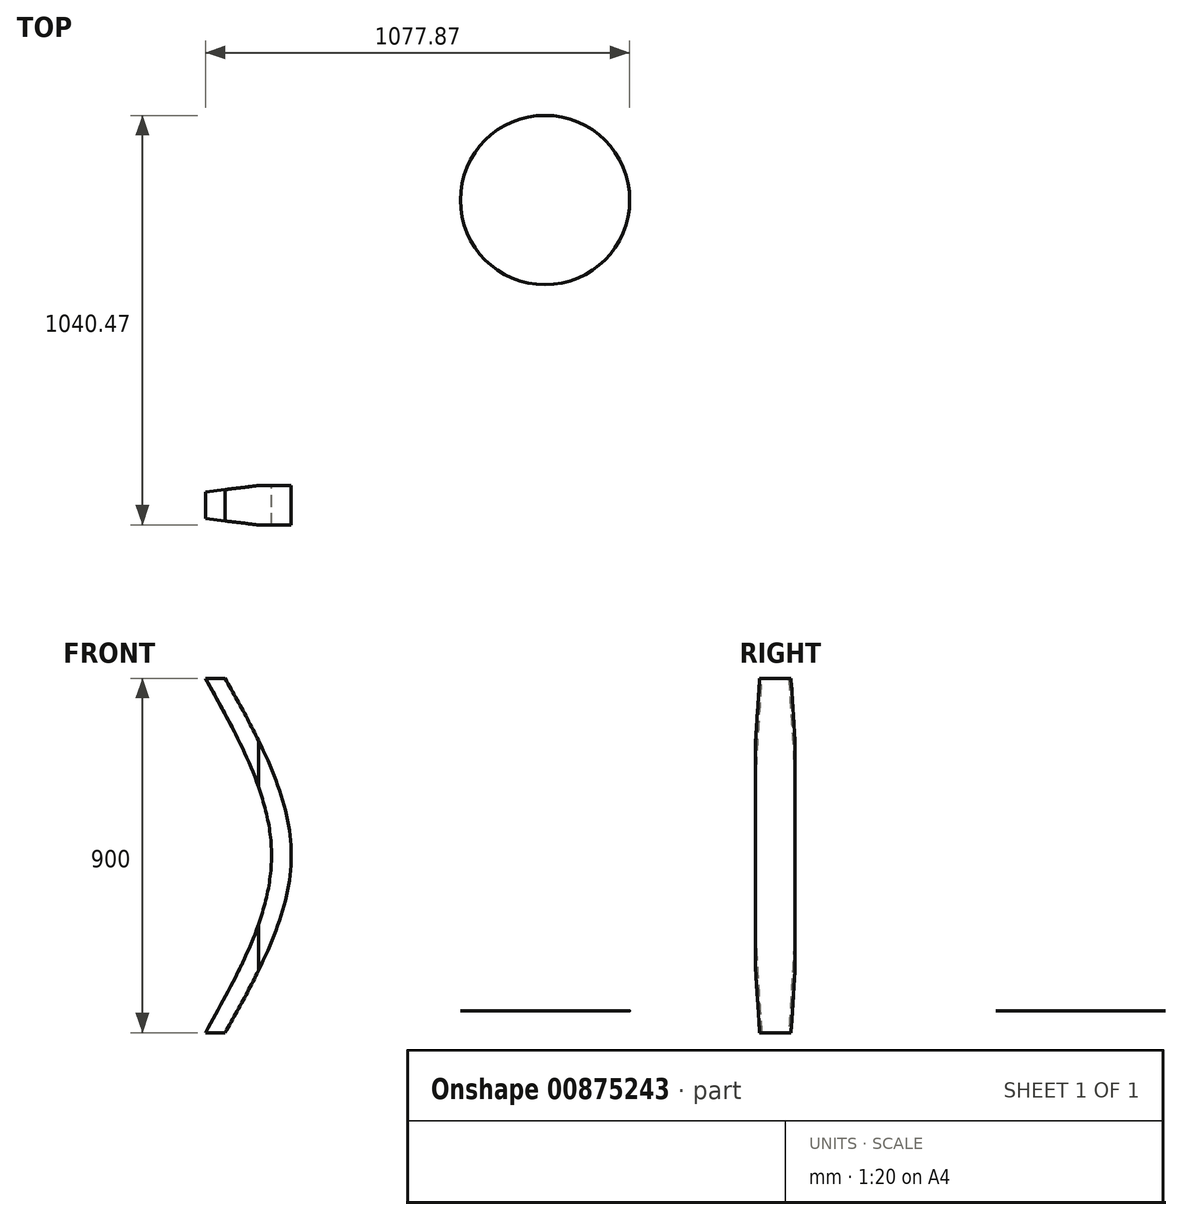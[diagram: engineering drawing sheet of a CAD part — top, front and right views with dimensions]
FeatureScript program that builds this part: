
annotation { "Feature Type Name" : "Feature", "Feature Type Description" : "" }
export const myFeature = defineFeature(function(context is Context, id is Id, definition is map)
    precondition{}
    {
        {
            var Q0;
            Q0=qCreatedBy(makeId("Right.planeOp"),FACE);
            var sketch = newSketch(context, id + "F0", { "sketchPlane" : qUnion([Q0])});
            skLineSegment(sketch, "E0.bottom", {"start": v(-21.22, 845.17) * mm, "end": v(78.78, 845.17) * mm});
            skLineSegment(sketch, "E0.top", {"start": v(-21.22, -54.83) * mm, "end": v(78.78, -54.83) * mm});
            skLineSegment(sketch, "E0.left", {"start": v(-21.22, 845.17) * mm, "end": v(-21.22, -54.83) * mm});
            skLineSegment(sketch, "E0.right", {"start": v(78.78, 845.17) * mm, "end": v(78.78, -54.83) * mm});
            skSolve(sketch);
        }
        {
            var Q0;
            Q0 = qSketchRegion(id + "F0", true);
            extrude(context, id + "F1", {"entities" : qUnion([Q0]), "depth" : 187.9 * mm, "offsetDistance" : 25 * mm});
        }
        {
            var Q0;
            Q0=makeQuery(id+"F1.opExtrude","CAP_FACE",FACE,{"disambiguationData":[OSD([sQuery(id+"F0.wireOp",EDGE,"E0.bottom"),sQuery(id+"F0.wireOp",EDGE,"E0.top"),sQuery(id+"F0.wireOp",EDGE,"E0.left"),sQuery(id+"F0.wireOp",EDGE,"E0.right")])],"isStart":true});
            extrude(context, id + "F2", {"entities" : qUnion([Q0]), "operationType" : NewBodyOperationType.ADD, "depth" : 30 * mm, "offsetDistance" : 25 * mm});
        }
        {
            var Q0;
            Q0=makeQuery(id+"F1.opExtrude","SWEPT_FACE",FACE,{"disambiguationData":[OSD([sQuery(id+"F0.wireOp",EDGE,"E0.right")])]});
            var sketch = newSketch(context, id + "F3", { "sketchPlane" : qUnion([Q0])});
            skLineSegment(sketch, "E1", {"start": v(-187.9, 395.17) * mm, "end": v(0, 395.17) * mm});
            skLineSegment(sketch, "E2", {"start": v(-187.9, 845.17) * mm, "end": v(-20, 845.17) * mm});
            skLineSegment(sketch, "E3", {"start": v(-20, -54.83) * mm, "end": v(-187.9, -54.83) * mm});
            skLineSegment(sketch, "E4", {"start": v(-187.9, -54.83) * mm, "end": v(-187.9, 395.17) * mm});
            skLineSegment(sketch, "E5", {"start": v(-187.9, 845.17) * mm, "end": v(-187.9, 395.17) * mm});
            skLineSegment(sketch, "E6", {"start": v(0, -54.83) * mm, "end": v(-20, -54.83) * mm});
            skLineSegment(sketch, "E7", {"start": v(-187.9, 395.17) * mm, "end": v(-137.9, 395.17) * mm});
            skFitSpline(sketch, "E8", {"points": [v(-20, -54.83) * mm, v(-187.9, 395.17) * mm, v(-20, 845.17) * mm], "startDerivative": vector(-503.7, 900) * mm, "endDerivative": vector(503.7, 900) * mm});
            skLineSegment(sketch, "E9", {"start": v(-20, 845.17) * mm, "end": v(30, 845.17) * mm});
            skLineSegment(sketch, "E10", {"start": v(30, 845.17) * mm, "end": v(30, -54.83) * mm});
            skLineSegment(sketch, "E11", {"start": v(30, -54.83) * mm, "end": v(-20, -54.83) * mm});
            skFitSpline(sketch, "E12", {"points": [v(30, -54.83) * mm, v(-137.9, 395.17) * mm, v(30, 845.17) * mm], "startDerivative": vector(-503.7, 900) * mm, "endDerivative": vector(503.7, 900) * mm});
            skSolve(sketch);
        }
        {
            var Q0;
            {var subQ0=sQuery(id+"F3.wireOp",EDGE,"E2");Q0=makeQuery(id+"F3.imprint","IMPRINT",FACE,{"disambiguationData":[TD([[makeQuery(id+"F3.imprint","IMPRINT",EDGE,{"derivedFrom":subQ0}),-1.0]])]});}
            var Q1;
            {var subQ0=sQuery(id+"F3.wireOp",EDGE,"E3");Q1=makeQuery(id+"F3.imprint","IMPRINT",FACE,{"disambiguationData":[TD([[makeQuery(id+"F3.imprint","IMPRINT",EDGE,{"derivedFrom":subQ0}),1.0]])]});}
            var Q2;
            {var subQ0=sQuery(id+"F3.wireOp",EDGE,"E10");Q2=makeQuery(id+"F3.imprint","IMPRINT",FACE,{"disambiguationData":[TD([[makeQuery(id+"F3.imprint","IMPRINT",EDGE,{"derivedFrom":subQ0}),-1.0]])]});}
            extrude(context, id + "F4", {"entities" : qUnion([Q0, Q1, Q2]), "operationType" : NewBodyOperationType.REMOVE, "oppositeDirection" : true, "depth" : 600 * mm, "offsetDistance" : 25 * mm});
        }
        {
            var Q0;
            {var subQ0=sQuery(id+"F0.wireOp",EDGE,"E0.bottom");Q0=makeQuery(id+"F2.boolean.opBoolean","MERGE",FACE,{"derivedFrom":[makeQuery(id+"F1.opExtrude","SWEPT_FACE",FACE,{"disambiguationData":[OSD([subQ0])]}),makeQuery(id+"F2.opExtrude","SWEPT_FACE",FACE,{"disambiguationData":[OSD([subQ0])]})]});}
            var sketch = newSketch(context, id + "F5", { "sketchPlane" : qUnion([Q0])});
            skLineSegment(sketch, "E13", {"start": v(-30, 28.78) * mm, "end": v(-30, 62.53) * mm});
            skLineSegment(sketch, "E14", {"start": v(-30, 28.78) * mm, "end": v(-30, -4.98) * mm});
            skLineSegment(sketch, "E15", {"start": v(319.35, 247.93) * mm, "end": v(319.35, -262.5) * mm});
            skLineSegment(sketch, "E16", {"start": v(-30, -4.98) * mm, "end": v(-30, -262.5) * mm});
            skLineSegment(sketch, "E17", {"start": v(-30, -262.5) * mm, "end": v(319.35, -262.5) * mm});
            skLineSegment(sketch, "E18", {"start": v(319.35, 247.93) * mm, "end": v(-30, 247.93) * mm});
            skLineSegment(sketch, "E19", {"start": v(-30, 247.93) * mm, "end": v(-30, 62.53) * mm});
            skLineSegment(sketch, "E20", {"start": v(20, 28.78) * mm, "end": v(187.9, 28.78) * mm});
            skLineSegment(sketch, "E21", {"start": v(187.9, 28.78) * mm, "end": v(187.9, -31.22) * mm});
            skLineSegment(sketch, "E22", {"start": v(187.9, -31.22) * mm, "end": v(187.9, 88.78) * mm});
            skLineSegment(sketch, "E23", {"start": v(187.9, 88.78) * mm, "end": v(-30, 62.53) * mm});
            skLineSegment(sketch, "E24", {"start": v(-30, -4.98) * mm, "end": v(187.9, -31.22) * mm});
            skSolve(sketch);
        }
        {
            var Q0;
            {var subQ1=sQuery(id+"F0.wireOp",EDGE,"E0.right");var subQ2=sQuery(id+"F0.wireOp",EDGE,"E0.bottom");var subQ3=makeQuery(id+"F2.boolean.opBoolean","MERGE",EDGE,{"derivedFrom":[makeQuery(id+"F1.opExtrude","SWEPT_EDGE",EDGE,{"disambiguationData":[OSD([subQ2,subQ1])]}),makeQuery(id+"F2.opExtrude","SWEPT_EDGE",EDGE,{"disambiguationData":[OSD([subQ2,subQ1])]})]});Q0=makeQuery(id+"F5.imprint","IMPRINT",FACE,{"disambiguationData":[TD([[makeQuery(id+"F5.imprint","IMPRINT",EDGE,{"derivedFrom":subQ3}),1.0]])]});}
            var Q1;
            {var subQ1=sQuery(id+"F0.wireOp",EDGE,"E0.left");var subQ2=sQuery(id+"F0.wireOp",EDGE,"E0.bottom");var subQ3=makeQuery(id+"F2.boolean.opBoolean","MERGE",EDGE,{"derivedFrom":[makeQuery(id+"F1.opExtrude","SWEPT_EDGE",EDGE,{"disambiguationData":[OSD([subQ2,subQ1])]}),makeQuery(id+"F2.opExtrude","SWEPT_EDGE",EDGE,{"disambiguationData":[OSD([subQ2,subQ1])]})]});Q1=makeQuery(id+"F5.imprint","IMPRINT",FACE,{"disambiguationData":[TD([[makeQuery(id+"F5.imprint","IMPRINT",EDGE,{"derivedFrom":subQ3}),-1.0]])]});}
            var Q2;
            Q2=makeQuery(id+"F5.imprint","IMPRINT",FACE,{"disambiguationData":[TD([[makeQuery(id+"F5.imprint","IMPRINT",EDGE,{"derivedFrom":sQuery(id+"F5.wireOp",EDGE,"E15")}),-1.0]])]});
            extrude(context, id + "F6", {"entities" : qUnion([Q0, Q1, Q2]), "operationType" : NewBodyOperationType.REMOVE, "oppositeDirection" : true, "depth" : 995 * mm, "offsetDistance" : 25 * mm});
        }
        {
            var Q0;
            Q0=qCreatedBy(makeId("Top.planeOp"),FACE);
            var sketch = newSketch(context, id + "F7", { "sketchPlane" : qUnion([Q0])});
            skCircle(sketch, "E25", {"center": v(832.87, 804.25) * mm, "radius": 215 * mm});
            skSolve(sketch);
        }
        {
            var Q0;
            Q0 = qSketchRegion(id + "F7", true);
            extrude(context, id + "F8", {"entities" : qUnion([Q0]), "operationType" : NewBodyOperationType.ADD, "depth" : 1 * mm, "offsetDistance" : 25 * mm});
        }
    });
